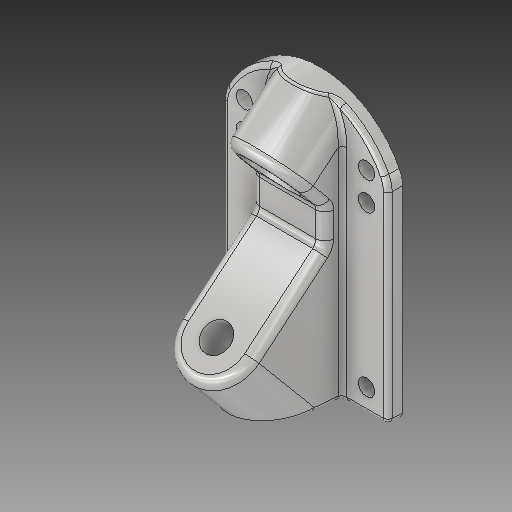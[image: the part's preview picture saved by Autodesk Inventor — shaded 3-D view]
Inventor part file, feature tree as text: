
AUTODESK INVENTOR PART (.ipt)
format: ipt  version: 2019 (Build 230136000, 136)  size: 453,632 bytes
history: native  units: mm
features: sketch x10, extrude x9, other x6, fillet x5, projected_geometry x4, revolve x1
ambient origin geometry x8: Origin, YZ Plane, XZ Plane, XY Plane, X Axis, Y Axis, Z Axis, Center Point
bodies: Body1 (feature_tree)
feature tree (35):
  other  "Твердое тело1"
  extrude  "Выдавливание1"  Depth=55.6mm
  other  "РабПлоскость1"
  extrude  "Выдавливание2"  Depth=88.5mm
  extrude  "Выдавливание3"  Depth=54.0mm
  fillet  "Сопряжение1"  Radius=63.5mm
  extrude  "Выдавливание4"  Depth=41.3mm
  other  "РабПлоскость3"
  other  "НаклГрань1"
  extrude  "Выдавливание5"  Depth=5.5mm
  extrude  "Выдавливание6"  Depth=5.0mm TaperAngle=0.0deg
  extrude  "Выдавливание7"  Depth=8.726646mm
  extrude  "Выдавливание8"  Depth=6.0mm
  fillet  "Сопряжение2"  Radius=25.0mm
  fillet  "Сопряжение3"  Radius=25.0mm
  fillet  "Сопряжение4"  Radius=12.5mm
  other  "РабПлоскость4"
  revolve  "Вращение1"
  extrude  "Выдавливание9"  Depth=18.0mm
  fillet  "Сопряжение7"  Radius=15.0mm
  sketch  "Эскиз1"
  sketch  "Эскиз2"
  sketch  "Эскиз3"
  sketch  "Эскиз4"
  projected_geometry  "Спроецированная петля1"
  sketch  "Эскиз5"
  projected_geometry  "Спроецированная петля2"
  sketch  "Эскиз6"
  sketch  "Эскиз7"
  projected_geometry  "Спроецированная петля3"
  sketch  "Эскиз8"
  projected_geometry  "Спроецированная петля4"
  other  "РабОсь1"
  sketch  "Эскиз9"
  sketch  "Эскиз10"
